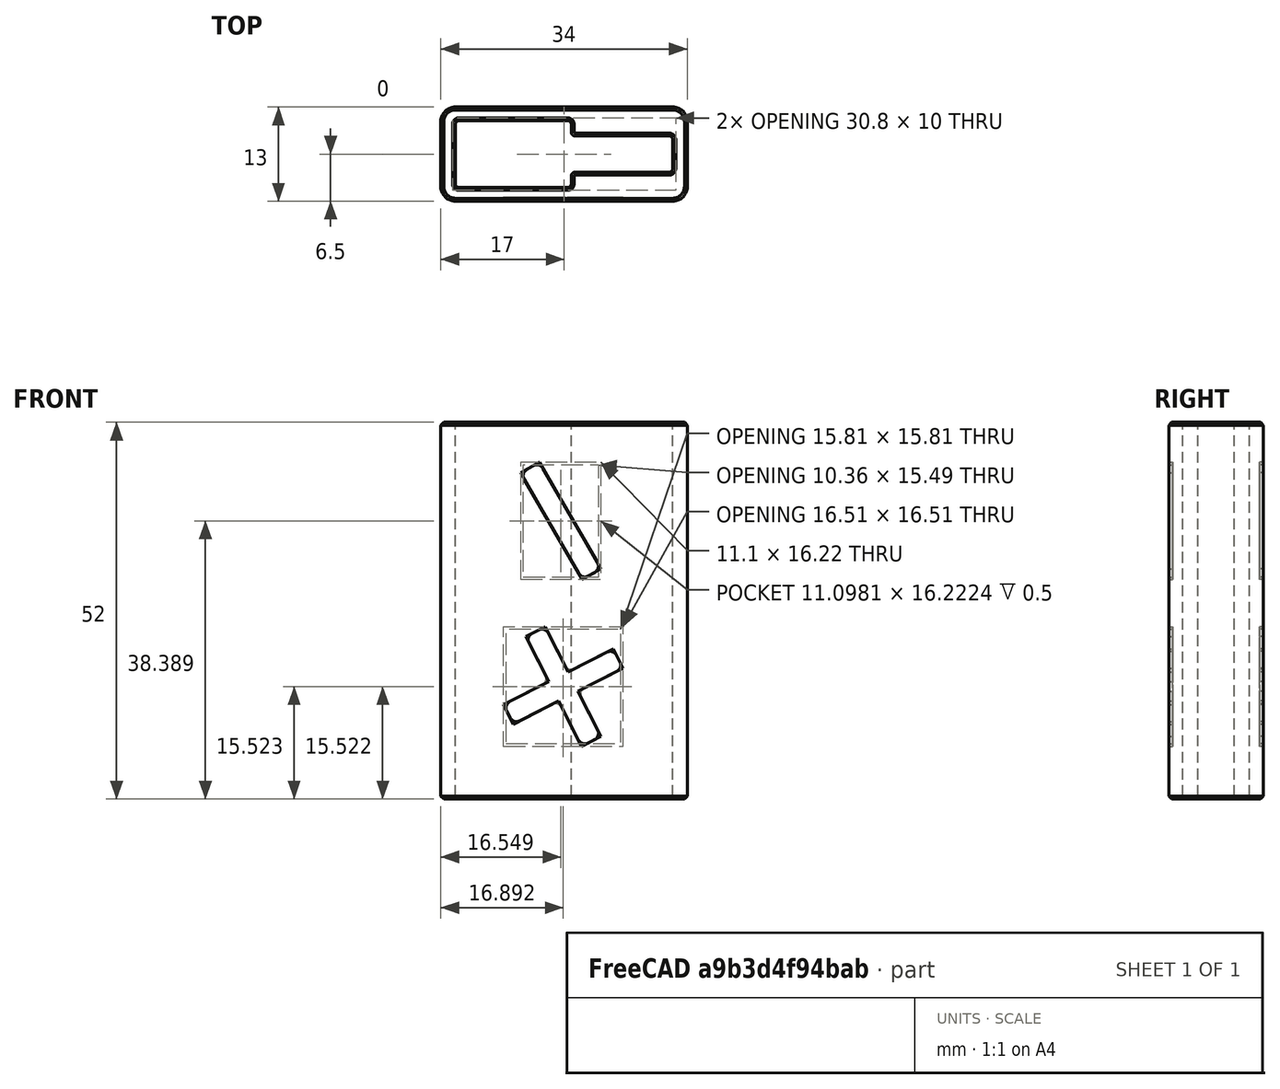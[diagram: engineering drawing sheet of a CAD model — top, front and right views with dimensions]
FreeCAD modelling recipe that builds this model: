
FCSTD DOCUMENT  (FreeCAD 0.17R13522 (Git))
Label: lidl_taco_puntas_estrella_planas
License: All rights reserved
LicenseURL: http://en.wikipedia.org/wiki/All_rights_reserved
objects: Part::Box×3, Part::Fillet×3, Mesh::Feature×1, Part::Fuse×1, Part::Cut×1, Part::Chamfer×1, PartDesign::FeatureBase×1, Sketcher::SketchObject×1, PartDesign::Pocket×1, PartDesign::Mirrored×1, PartDesign::Body×1
note: 15 computed .brp shape members not serialized (recipe doc carries the construction recipe); baked Part::Feature solids carry a one-line shape summary decoded from their .brp

FEATURE [Mesh::Feature] lidl
FEATURE [Part::Box] Box  label="Cubo"
  AttacherType = Attacher::AttachEngine3D
  Height = 60
  Length = 16
  Placement = pos=(0,-4.6,0) rot=(0,0,1;0rad)
  Width = 9.2
FEATURE [Part::Box] Box001  label="Cubo001"
  AttacherType = Attacher::AttachEngine3D
  Height = 60
  Length = 30
  Placement = pos=(0,-2.5,0) rot=(0,0,1;0rad)
  Width = 5
FEATURE [Part::Fuse] Fusion
  Base = -> Box
  Refine = true
  Tool = -> Box001
FEATURE [Part::Fillet] Fillet
  Base = -> Fusion
  Edges = 8 edges r=0.5: [Edge2,Edge4,Edge6,Edge9,Edge12,Edge16,Edge18,Edge20]
FEATURE [Part::Box] Box002  label="Cubo002"
  AttacherType = Attacher::AttachEngine3D
  Height = 52
  Length = 34
  Placement = pos=(-2,-6.5,0) rot=(0,0,1;0rad)
  Width = 13
FEATURE [Part::Cut] Cut
  Base = -> Box002
  Refine = true
  Tool = -> Fillet
FEATURE [Part::Fillet] Fillet001
  Base = -> Cut
  Edges = 4 edges r=2: [Edge1,Edge3,Edge6,Edge27]
FEATURE [Part::Chamfer] Chamfer
  Base = -> Fillet001
  Edges = 48 edges r=0.4: [Edge1,Edge4,Edge5,Edge6,Edge7,Edge8,Edge9,Edge10,Edge11,Edge12,Edge13,Edge14,Edge15,Edge16,Edge17,Edge18,Edge19,Edge20,Edge21,Edge22,Edge23,Edge24,Edge25,Edge26,Edge27,Edge28,Edge30,Edge32,Edge33,Edge34,Edge35,Edge36,Edge37,Edge38,Edge39,Edge40,Edge41,Edge42,Edge43,Edge44,Edge45,Edge46,Edge47,+5 more]
FEATURE [PartDesign::FeatureBase] BaseFeature
  BaseFeature = -> Chamfer
FEATURE [Sketcher::SketchObject] Sketch
  MapMode = 5
  Placement = pos=(0,-6.5,0) rot=(1,0,0;1.5708rad)
  Support = -> [BaseFeature]
  sketch-geometry (20):
    g0: LineSegment StartX=9 StartY=45 StartZ=0 EndX=11.5981 EndY=46.5 EndZ=0
    g1: LineSegment StartX=11.5981 StartY=46.5 StartZ=0 EndX=20.0981 EndY=31.7776 EndZ=0
    g2: LineSegment StartX=20.0981 StartY=31.7776 StartZ=0 EndX=17.5 EndY=30.2776 EndZ=0
    g3: LineSegment StartX=17.5 StartY=30.2776 StartZ=0 EndX=9 EndY=45 EndZ=0
    g4: LineSegment StartX=9.69714 StartY=22.415 StartZ=0 EndX=12.3702 EndY=23.777 EndZ=0
    g5: LineSegment StartX=12.3702 StartY=23.777 StartZ=0 EndX=15.5481 EndY=17.5399 EndZ=0
    g6: LineSegment StartX=20.088 StartY=8.62984 StartZ=0 EndX=17.415 EndY=7.26787 EndZ=0
    g7: LineSegment StartX=17.415 StartY=7.26787 StartZ=0 EndX=14.237 EndY=13.5049 EndZ=0
    g8: LineSegment StartX=21.7851 StartY=20.7178 StartZ=0 EndX=23.1471 EndY=18.0448 EndZ=0
    g9: LineSegment StartX=23.1471 StartY=18.0448 StartZ=0 EndX=16.9101 EndY=14.8669 EndZ=0
    g10: LineSegment StartX=8 StartY=10.327 StartZ=0 EndX=6.63803 EndY=13 EndZ=0
    g11: LineSegment StartX=6.63803 StartY=13 StartZ=0 EndX=12.8751 EndY=16.1779 EndZ=0
    g12: LineSegment [constr] StartX=6.63803 StartY=13 StartZ=0 EndX=9.69714 EndY=22.415 EndZ=0
    g13: LineSegment [constr] StartX=12.3702 StartY=23.777 StartZ=0 EndX=21.7851 EndY=20.7178 EndZ=0
    g14: LineSegment [constr] StartX=23.1471 StartY=18.0448 StartZ=0 EndX=20.088 EndY=8.62984 EndZ=0
    g15: LineSegment [constr] StartX=17.415 StartY=7.26787 StartZ=0 EndX=8 EndY=10.327 EndZ=0
    g16: LineSegment StartX=15.5481 StartY=17.5399 StartZ=0 EndX=21.7851 EndY=20.7178 EndZ=0
    g17: LineSegment StartX=16.9101 StartY=14.8669 StartZ=0 EndX=20.088 EndY=8.62984 EndZ=0
    g18: LineSegment StartX=12.8751 StartY=16.1779 StartZ=0 EndX=9.69714 EndY=22.415 EndZ=0
    g19: LineSegment StartX=14.237 StartY=13.5049 StartZ=0 EndX=8 EndY=10.327 EndZ=0
  constraints (53):
    c: Coincident(g0,g1)
    c: Coincident(g1,g2)
    c: Coincident(g2,g3)
    c: Coincident(g3,g0)
    c: Perpendicular(g0,g3)
    c: Perpendicular(g1,g2)
    c: Perpendicular(g2,g3)
    c: Distance(g2) = 3
    c: Distance(g3) = 17
    c: Angle(g-2,g3) = 0.523599
    c: DistanceX(g-1,g0) = 9
    c: DistanceY(g-1,g0) = 45
    c: Coincident(g4,g5)
    c: Coincident(g17,g6)
    c: Coincident(g6,g7)
    c: Coincident(g18,g4)
    c: Perpendicular(g4,g7)
    c: Perpendicular(g5,g6)
    c: Perpendicular(g6,g7)
    c: Equal(g2,g6) = 3
    c: Coincident(g8,g9)
    c: Coincident(g19,g10)
    c: Coincident(g10,g11)
    c: Coincident(g16,g8)
    c: Perpendicular(g8,g11)
    c: Perpendicular(g9,g10)
    c: Perpendicular(g10,g11)
    c: Distance(g8) = 3
    c: Perpendicular(g5,g9)
    c: Coincident(g10,g12)
    c: Coincident(g12,g4)
    c: Coincident(g13,g4)
    c: Coincident(g13,g8)
    c: Coincident(g14,g8)
    c: Coincident(g14,g17)
    c: Coincident(g15,g6)
    c: Coincident(g15,g19)
    c: Equal(g12,g13)
    c: Equal(g13,g14)
    c: Equal(g14,g15)
    c: Angle(g12,g-2) = 0.314159
    c: DistanceX(g-1,g19) = 8
    c: DistanceY(g-1,g10) = 13
    c: Tangent(g11,g16)
    c: Coincident(g5,g16)
    c: Tangent(g5,g17)
    c: Coincident(g18,g11)
    c: Tangent(g7,g18)
    c: Coincident(g9,g17)
    c: Coincident(g19,g7)
    c: Tangent(g9,g19)
    c: Equal(g5,g16)
    c: Distance(g6,g4) = 17
FEATURE [PartDesign::Pocket] Pocket
  BaseFeature = -> BaseFeature
  Length = 0.5
  Length2 = 100
  Profile = -> Sketch
  Refine = true
  Type = 0
FEATURE [PartDesign::Mirrored] Mirrored
  BaseFeature = -> Pocket
  MirrorPlane = -> XZ_Plane
  Originals = -> [Pocket]
  Refine = true
FEATURE [PartDesign::Body] Body
  BaseFeature = -> Chamfer
  Group = -> [BaseFeature,Sketch,Pocket,Mirrored]
  Origin = -> Origin
  Tip = -> Mirrored
FEATURE [Part::Fillet] Fillet002
  Base = -> Mirrored
  Edges = 28 edges r=1: [Edge110,Edge112,Edge116,Edge118,Edge122,Edge124,Edge128,Edge130,Edge134,Edge136,Edge138,Edge140,Edge217,Edge219,Edge221,Edge223,Edge225,Edge227,Edge229,Edge231,Edge233,Edge235,Edge237,Edge239,Edge241,Edge243,Edge245,Edge247]
